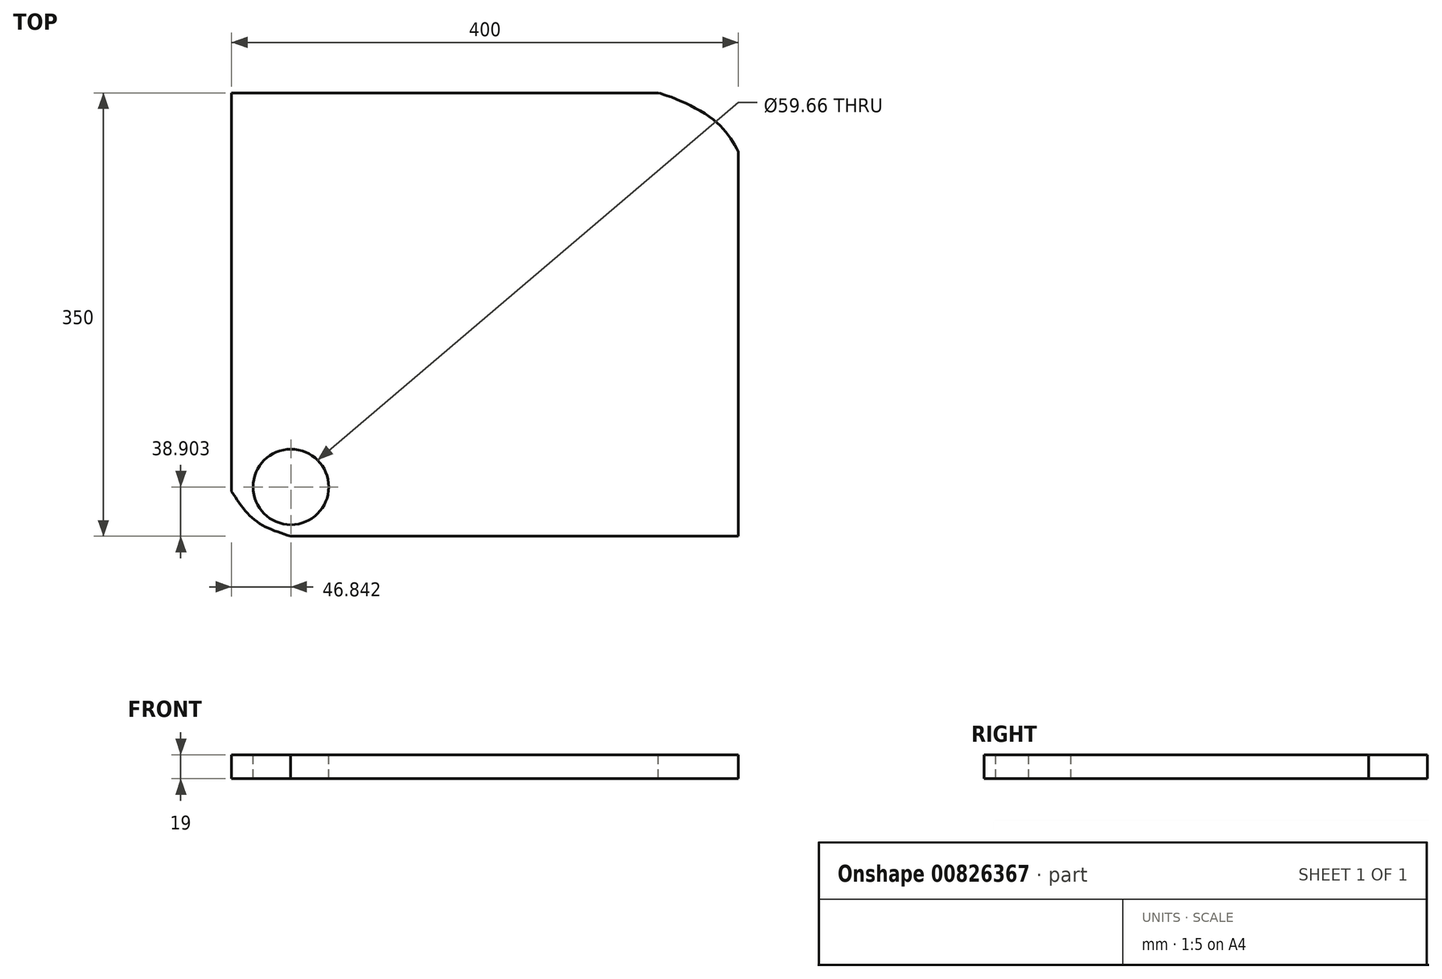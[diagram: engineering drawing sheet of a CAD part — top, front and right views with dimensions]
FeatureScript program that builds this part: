
annotation { "Feature Type Name" : "Feature", "Feature Type Description" : "" }
export const myFeature = defineFeature(function(context is Context, id is Id, definition is map)
    precondition{}
    {
        {
            var Q0;
            Q0=qCreatedBy(makeId("Top.planeOp"),FACE);
            var sketch = newSketch(context, id + "F0", { "sketchPlane" : qUnion([Q0])});
            skLineSegment(sketch, "E0.bottom", {"start": v(-200, 175) * mm, "end": v(200, 175) * mm});
            skLineSegment(sketch, "E0.top", {"start": v(-200, -175) * mm, "end": v(200, -175) * mm});
            skLineSegment(sketch, "E0.left", {"start": v(-200, 175) * mm, "end": v(-200, -175) * mm});
            skLineSegment(sketch, "E0.right", {"start": v(200, 175) * mm, "end": v(200, -175) * mm});
            skPoint(sketch, "E0.middle", {"position": v(0, 0) * mm});
            skSolve(sketch);
        }
        {
            var Q0;
            Q0=makeQuery(id+"F0.imprint","IMPRINT",FACE,{"disambiguationData":[TD([[makeQuery(id+"F0.imprint","IMPRINT",EDGE,{"derivedFrom":sQuery(id+"F0.wireOp",EDGE,"E0.bottom")}),-1.0]])]});
            extrude(context, id + "F1", {"entities" : qUnion([Q0]), "depth" : 19 * mm, "offsetDistance" : 25 * mm});
        }
        {
            var Q0;
            Q0=makeQuery(id+"F1.opExtrude","CAP_FACE",FACE,{"disambiguationData":[OSD([sQuery(id+"F0.wireOp",EDGE,"E0.bottom"),sQuery(id+"F0.wireOp",EDGE,"E0.top"),sQuery(id+"F0.wireOp",EDGE,"E0.left"),sQuery(id+"F0.wireOp",EDGE,"E0.right")])],"isStart":false});
            var sketch = newSketch(context, id + "F2", { "sketchPlane" : qUnion([Q0])});
            skFitSpline(sketch, "E1", {"points": [v(-153.55, -175) * mm, v(-181, -162.77) * mm, v(-200, -139.63) * mm], "startDerivative": vector(-59.07, 18.97) * mm, "endDerivative": vector(-33.83, 51.8) * mm});
            skSolve(sketch);
        }
        {
            var Q0;
            {var subQ0=sQuery(id+"F2.wireOp",EDGE,"E1");Q0=makeQuery(id+"F2.imprint","IMPRINT",FACE,{"disambiguationData":[TD([[makeQuery(id+"F2.imprint","IMPRINT",EDGE,{"derivedFrom":subQ0}),1.0]])]});}
            extrude(context, id + "F3", {"entities" : qUnion([Q0]), "operationType" : NewBodyOperationType.REMOVE, "endBound" : BoundingType.THROUGH_ALL, "oppositeDirection" : true, "depth" : 25 * mm, "offsetDistance" : 25 * mm});
        }
        {
            var Q0;
            Q0=makeQuery(id+"F1.opExtrude","CAP_FACE",FACE,{"disambiguationData":[OSD([sQuery(id+"F0.wireOp",EDGE,"E0.bottom"),sQuery(id+"F0.wireOp",EDGE,"E0.top"),sQuery(id+"F0.wireOp",EDGE,"E0.left"),sQuery(id+"F0.wireOp",EDGE,"E0.right")])],"isStart":false});
            var sketch = newSketch(context, id + "F4", { "sketchPlane" : qUnion([Q0])});
            skFitSpline(sketch, "E2", {"points": [v(200, 128.64) * mm, v(177.87, 155.7) * mm, v(136.68, 175) * mm, v(133.55, 175) * mm], "startDerivative": vector(-38.63, 68.23) * mm, "endDerivative": vector(-17.23, -4.03) * mm});
            skSolve(sketch);
        }
        {
            var Q0;
            {var subQ0=sQuery(id+"F4.wireOp",EDGE,"E2");var subQ1=makeQuery(id+"F1.opExtrude","CAP_EDGE",EDGE,{"disambiguationData":[OSD([sQuery(id+"F0.wireOp",EDGE,"E0.right")])],"isStart":false});var subQ2=makeQuery(id+"F4.imprint","INTERSECT",VERTEX,{"derivedFrom":[subQ1,subQ0]});Q0=makeQuery(id+"F4.imprint","IMPRINT",FACE,{"disambiguationData":[TD([[makeQuery(id+"F4.imprint","IMPRINT",EDGE,{"disambiguationData":[TD([[subQ2,-1.0]])],"derivedFrom":subQ0}),-1.0]])]});}
            extrude(context, id + "F5", {"entities" : qUnion([Q0]), "operationType" : NewBodyOperationType.REMOVE, "endBound" : BoundingType.THROUGH_ALL, "oppositeDirection" : true, "depth" : 25 * mm, "offsetDistance" : 25 * mm});
        }
        {
            var Q0;
            Q0=makeQuery(id+"F1.opExtrude","CAP_FACE",FACE,{"disambiguationData":[OSD([sQuery(id+"F0.wireOp",EDGE,"E0.bottom"),sQuery(id+"F0.wireOp",EDGE,"E0.top"),sQuery(id+"F0.wireOp",EDGE,"E0.left"),sQuery(id+"F0.wireOp",EDGE,"E0.right")])],"isStart":false});
            var sketch = newSketch(context, id + "F6", { "sketchPlane" : qUnion([Q0])});
            skCircle(sketch, "E3", {"center": v(-153.16, -136.1) * mm, "radius": 29.83 * mm});
            skSolve(sketch);
        }
        {
            var Q0;
            Q0=makeQuery(id+"F6.imprint","IMPRINT",FACE,{"disambiguationData":[TD([[makeQuery(id+"F6.imprint","IMPRINT",EDGE,{"derivedFrom":sQuery(id+"F6.wireOp",EDGE,"E3")}),1.0]])]});
            extrude(context, id + "F7", {"entities" : qUnion([Q0]), "operationType" : NewBodyOperationType.REMOVE, "endBound" : BoundingType.THROUGH_ALL, "oppositeDirection" : true, "depth" : 25 * mm, "offsetDistance" : 25 * mm});
        }
    });
